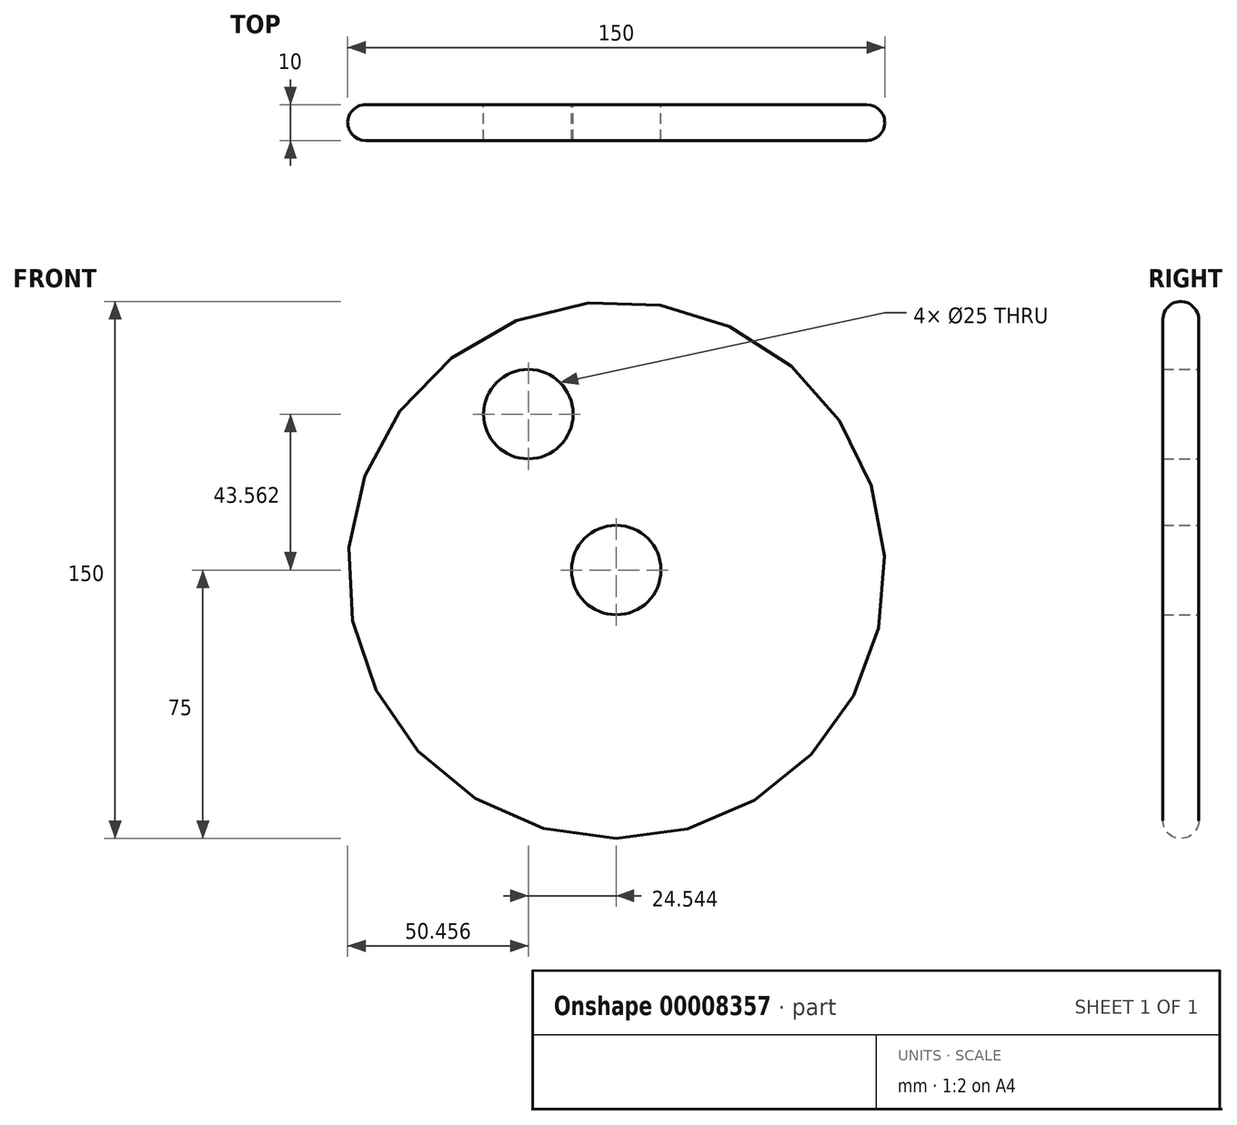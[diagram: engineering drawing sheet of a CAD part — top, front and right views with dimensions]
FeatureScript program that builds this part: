
annotation { "Feature Type Name" : "Feature", "Feature Type Description" : "" }
export const myFeature = defineFeature(function(context is Context, id is Id, definition is map)
    precondition{}
    {
        {
            var Q0;
            Q0=qCreatedBy(makeId("Front.planeOp"),FACE);
            var sketch = newSketch(context, id + "F0", { "sketchPlane" : qUnion([Q0])});
            skCircle(sketch, "E0", {"center": v(0, 0) * mm, "radius": 75 * mm});
            skCircle(sketch, "E1", {"center": v(33.43, 37.18) * mm, "radius": 12.5 * mm});
            skSolve(sketch);
        }
        {
            var Q0;
            Q0=makeQuery(id+"F0.imprint","IMPRINT",FACE,{"disambiguationData":[TD([[makeQuery(id+"F0.imprint","IMPRINT",EDGE,{"derivedFrom":sQuery(id+"F0.wireOp",EDGE,"E0")}),1.0]])]});
            extrude(context, id + "F1", {"entities" : qUnion([Q0]), "depth" : 10 * mm});
        }
        {
            var Q0;
            Q0=makeQuery(id+"F1.opExtrude","CAP_FACE",FACE,{"disambiguationData":[OSD([sQuery(id+"F0.wireOp",EDGE,"E0"),sQuery(id+"F0.wireOp",EDGE,"E1")])],"isStart":false});
            var sketch = newSketch(context, id + "F2", { "sketchPlane" : qUnion([Q0])});
            skCircle(sketch, "E2", {"center": v(0, 0) * mm, "radius": 12.5 * mm});
            skSolve(sketch);
        }
        {
            var Q0;
            Q0=makeQuery(id+"F2.imprint","IMPRINT",FACE,{"disambiguationData":[TD([[makeQuery(id+"F2.imprint","IMPRINT",EDGE,{"derivedFrom":sQuery(id+"F2.wireOp",EDGE,"E2")}),1.0]])]});
            extrude(context, id + "F3", {"entities" : qUnion([Q0]), "operationType" : NewBodyOperationType.REMOVE, "oppositeDirection" : true, "depth" : 10 * mm});
        }
        {
            var Q0;
            Q0=makeQuery(id+"F1.opExtrude","CAP_EDGE",EDGE,{"disambiguationData":[OSD([sQuery(id+"F0.wireOp",EDGE,"E0")])],"isStart":true});
            chamfer(context, id + "F4", {"entities" : qUnion([Q0]), "width" : 5 * mm, "tangentPropagation" : true});
        }
        {
            var Q0;
            Q0=makeQuery(id+"F1.opExtrude","SWEPT_BODY",BODY,{"disambiguationData":[OSD([sQuery(id+"F0.wireOp",EDGE,"E0"),sQuery(id+"F0.wireOp",EDGE,"E1")])]});
            deleteBodies(context, id + "F5", {"entities" : qUnion([Q0])});
        }
        {
            var Q0;
            Q0=qCreatedBy(makeId("Front.planeOp"),FACE);
            var sketch = newSketch(context, id + "F6", { "sketchPlane" : qUnion([Q0])});
            skCircle(sketch, "E3", {"center": v(0, 0) * mm, "radius": 75 * mm});
            skCircle(sketch, "E4", {"center": v(0, 0) * mm, "radius": 12.5 * mm});
            skCircle(sketch, "E5", {"center": v(-24.54, 43.56) * mm, "radius": 12.5 * mm});
            skSolve(sketch);
        }
        {
            var Q0;
            Q0=makeQuery(id+"F6.imprint","IMPRINT",FACE,{"disambiguationData":[TD([[makeQuery(id+"F6.imprint","IMPRINT",EDGE,{"derivedFrom":sQuery(id+"F6.wireOp",EDGE,"E3")}),1.0]])]});
            extrude(context, id + "F7", {"entities" : qUnion([Q0]), "depth" : 10 * mm});
        }
        {
            var Q0;
            Q0=makeQuery(id+"F7.opExtrude","CAP_EDGE",EDGE,{"disambiguationData":[OSD([sQuery(id+"F6.wireOp",EDGE,"E3")])],"isStart":false});
            var Q1;
            Q1=makeQuery(id+"F7.opExtrude","CAP_EDGE",EDGE,{"disambiguationData":[OSD([sQuery(id+"F6.wireOp",EDGE,"E3")])],"isStart":true});
            fillet(context, id + "F8", {"entities" : qUnion([Q0, Q1]), "radius" : 5 * mm, "tangentPropagation" : true, "allowEdgeOverflow" : false});
        }
    });
